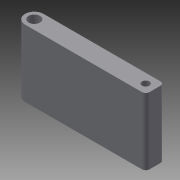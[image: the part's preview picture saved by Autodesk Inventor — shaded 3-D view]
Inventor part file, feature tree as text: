
AUTODESK INVENTOR PART (.ipt)
format: ipt  version: 2015 (Build 190159000, 159)  size: 98,304 bytes
history: native  units: mm
features: sketch x3, hole x2, fillet x2, extrude x1
ambient origin geometry x8: Origin, YZ Plane, XZ Plane, XY Plane, X Axis, Y Axis, Z Axis, Center Point
bodies: Solid1 (feature_tree)
feature tree (8):
  extrude  "Extrusion1"  Depth=5.0mm
  hole  "Hole1"  [1 undecoded]
  fillet  "Fillet1"  Radius=2.5mm
  fillet  "Fillet2"  Radius=1.0mm
  hole  "Hole2"  [1 undecoded]
  sketch  "Sketch1"  dims[d0=35.0mm d1=5.0mm]
  sketch  "Sketch2"  dims[d2=18.0mm d3=0.0mm d4=2.5mm d5=2.5mm]
  sketch  "Sketch3"  dims[d6=3.1mm d7=6.0mm d8=4.0mm d9=2.0mm d10=90.0deg d11=8.0mm d12=20.594885mm d13=1.0mm d14=2.5mm d15=2.5mm d16=2.5mm d17=5.0mm d18=2.0mm d19=6.0mm d20=4.0mm d21=2.0mm d22=90.0deg d23=11.0mm d24=20.594885mm]
note: 2 required parameter values undecoded (feature->parameter linkage not recoverable at this tier; creation-order binding heuristic only, values carry confidence <= 0.55)
